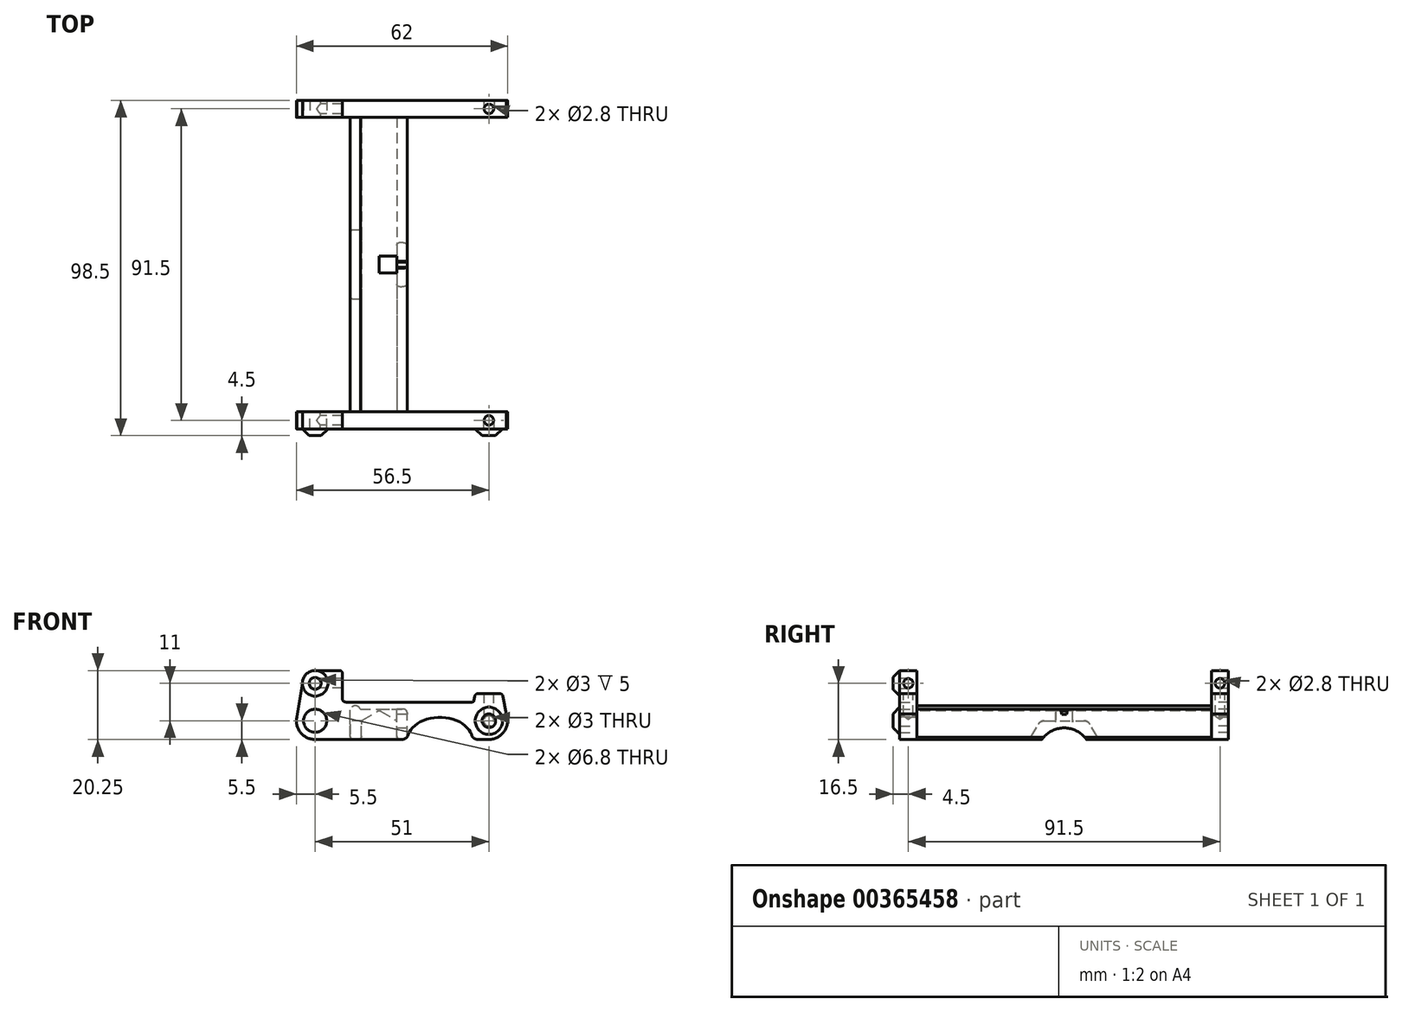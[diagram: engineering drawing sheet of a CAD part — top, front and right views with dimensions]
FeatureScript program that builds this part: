
annotation { "Feature Type Name" : "Feature", "Feature Type Description" : "" }
export const myFeature = defineFeature(function(context is Context, id is Id, definition is map)
    precondition{}
    {
        {
            var Q0;
            Q0=qCreatedBy(makeId("Front.planeOp"),FACE);
            var sketch = newSketch(context, id + "F0", { "sketchPlane" : qUnion([Q0])});
            skCircle(sketch, "E0", {"center": v(0, 0) * mm, "radius": 3.4 * mm});
            skCircle(sketch, "E1", {"center": v(0, 11) * mm, "radius": 1.5 * mm});
            skCircle(sketch, "E2", {"center": v(51, 0) * mm, "radius": 1.5 * mm});
            skArc(sketch, "E3", {"start": v(-5.35, 1.3) * mm, "mid": v(-4.32, -3.4) * mm, "end": v(0, -5.5) * mm});
            skLineSegment(sketch, "E4", {"start": v(0, -5.5) * mm, "end": v(51, -5.5) * mm});
            skArc(sketch, "E5", {"start": v(51, -5.5) * mm, "mid": v(56.5, 0) * mm, "end": v(51, 5.5) * mm});
            skLineSegment(sketch, "E6", {"start": v(9, 5.5) * mm, "end": v(46.12, 5.5) * mm});
            skPoint(sketch, "E7.orphan", {"position": v(0, 5.5) * mm});
            skPoint(sketch, "E8.orphan", {"position": v(-5.66, 0) * mm});
            skPoint(sketch, "E9.visualSharp", {"position": v(4.33, 5.5) * mm});
            skLineSegment(sketch, "E10", {"start": v(51, 1.5) * mm, "end": v(51, 5.5) * mm});
            skLineSegment(sketch, "E11", {"start": v(51, 0) * mm, "end": v(51, 8) * mm});
            skLineSegment(sketch, "E12", {"start": v(51, 8) * mm, "end": v(47.83, 8) * mm});
            skLineSegment(sketch, "E13", {"start": v(51, 8) * mm, "end": v(54.17, 8) * mm});
            skLineSegment(sketch, "E14", {"start": v(55.15, 7.18) * mm, "end": v(56.13, 2) * mm});
            skPoint(sketch, "E15.orphan", {"position": v(56.5, 0) * mm});
            skLineSegment(sketch, "E16.MirrorCS", {"start": v(46.85, 7.18) * mm, "end": v(46.6, 5.9) * mm});
            skPoint(sketch, "E17.visualSharp", {"position": v(55, 8) * mm});
            skArc(sketch, "E17.filletArc", {"start": v(55.15, 7.18) * mm, "mid": v(54.8, 7.77) * mm, "end": v(54.17, 8) * mm});
            skPoint(sketch, "E18.visualSharp", {"position": v(47, 8) * mm});
            skArc(sketch, "E18.filletArc", {"start": v(47.83, 8) * mm, "mid": v(47.2, 7.77) * mm, "end": v(46.85, 7.18) * mm});
            skPoint(sketch, "E19.orphan", {"position": v(45.87, 2) * mm});
            skArc(sketch, "E20.filletArc", {"start": v(46.12, 5.5) * mm, "mid": v(46.44, 5.62) * mm, "end": v(46.6, 5.9) * mm});
            skLineSegment(sketch, "E21", {"start": v(0, 11) * mm, "end": v(1.5, 11) * mm});
            skLineSegment(sketch, "E22", {"start": v(8, 11) * mm, "end": v(8, 14) * mm});
            skPoint(sketch, "E22.endSnap0", {"position": v(0, 14) * mm});
            skLineSegment(sketch, "E23", {"start": v(8, 11) * mm, "end": v(8, 6.5) * mm});
            skArc(sketch, "E24", {"start": v(0, 14.75) * mm, "mid": v(-2.65, 13.65) * mm, "end": v(-3.75, 11) * mm});
            skLineSegment(sketch, "E25", {"start": v(-3.75, 11) * mm, "end": v(-5.35, 1.3) * mm});
            skLineSegment(sketch, "E26", {"start": v(0, 11) * mm, "end": v(0, 14.75) * mm});
            skLineSegment(sketch, "E27", {"start": v(0, 14.75) * mm, "end": v(7.2, 14.75) * mm});
            skLineSegment(sketch, "E28", {"start": v(8, 13.95) * mm, "end": v(8, 11) * mm});
            skPoint(sketch, "E29.visualSharp", {"position": v(8, 14.75) * mm});
            skArc(sketch, "E29.filletArc", {"start": v(8, 13.95) * mm, "mid": v(7.77, 14.52) * mm, "end": v(7.2, 14.75) * mm});
            skPoint(sketch, "E30.visualSharp", {"position": v(8, 5.5) * mm});
            skArc(sketch, "E30.filletArc", {"start": v(8, 6.5) * mm, "mid": v(8.3, 5.8) * mm, "end": v(9, 5.5) * mm});
            skSolve(sketch);
        }
        {
            var Q0;
            Q0=qSketchRegion(id+"F0",true);
            extrude(context, id + "F1", {"entities" : qUnion([Q0]), "depth" : 5 * mm});
        }
        {
            var Q0;
            Q0=makeQuery(id+"F1.opExtrude","CAP_FACE",FACE,{"disambiguationData":[OSD([sQuery(id+"F0.wireOp",EDGE,"E0"),sQuery(id+"F0.wireOp",EDGE,"E1"),sQuery(id+"F0.wireOp",EDGE,"E2"),sQuery(id+"F0.wireOp",EDGE,"E3"),sQuery(id+"F0.wireOp",EDGE,"E4"),sQuery(id+"F0.wireOp",EDGE,"mQrOnHyL-yETB-5Hyz-XC6m-Qhvp57tjZrM2"),sQuery(id+"F0.wireOp",EDGE,"GuxY412t-x2rp-MWa2-55Ok-ayXwRCNW1Ffh"),sQuery(id+"F0.wireOp",EDGE,"Tq4Ys5zz-jUqY-a6fJ-V2RF-rb2bUuLUyHlJ"),sQuery(id+"F0.wireOp",EDGE,"E5"),sQuery(id+"F0.wireOp",EDGE,"E6"),sQuery(id+"F0.wireOp",EDGE,"E9.filletArc")])],"isStart":true});
            var sketch = newSketch(context, id + "F2", { "sketchPlane" : qUnion([Q0])});
            skLineSegment(sketch, "E31.MirrorCS", {"start": v(-25.5, 3.4) * mm, "end": v(-20.3, 3.4) * mm});
            skPoint(sketch, "E32.end.orphan", {"position": v(-27, 0) * mm});
            skPoint(sketch, "E32.start.orphan", {"position": v(-27, 3.4) * mm});
            skLineSegment(sketch, "E33", {"start": v(0, 0) * mm, "end": v(0, 3.4) * mm});
            skLineSegment(sketch, "E34", {"start": v(-27, -5.5) * mm, "end": v(-27, 3.4) * mm});
            skLineSegment(sketch, "E35", {"start": v(-24, -5.5) * mm, "end": v(-24, 0) * mm});
            skLineSegment(sketch, "E36", {"start": v(-27, -5.5) * mm, "end": v(-24, -5.5) * mm});
            skLineSegment(sketch, "E37", {"start": v(-24, 0) * mm, "end": v(-18.8, 3) * mm});
            skLineSegment(sketch, "E38", {"start": v(-27, 3.4) * mm, "end": v(-25.5, 3.4) * mm});
            skLineSegment(sketch, "E39", {"start": v(-20.3, 3.4) * mm, "end": v(-18.8, 3.4) * mm});
            skLineSegment(sketch, "E40.MirrorCS", {"start": v(-13.6, 0) * mm, "end": v(-18.8, 3) * mm});
            skLineSegment(sketch, "E41.MirrorCS", {"start": v(-13.6, -5.5) * mm, "end": v(-13.6, 0) * mm});
            skLineSegment(sketch, "E42.MirrorCS", {"start": v(-10.6, -5.5) * mm, "end": v(-13.6, -5.5) * mm});
            skLineSegment(sketch, "E43.MirrorCS", {"start": v(-10.3, -5.5) * mm, "end": v(-10.3, 3.4) * mm});
            skLineSegment(sketch, "E44.MirrorCS", {"start": v(-17.3, 3.4) * mm, "end": v(-18.8, 3.4) * mm});
            skArc(sketch, "E45", {"start": v(-10.3, 3.4) * mm, "mid": v(-11.8, 4.4) * mm, "end": v(-13.3, 3.4) * mm});
            skLineSegment(sketch, "E46.trimOffspring", {"start": v(-13.3, 3.4) * mm, "end": v(-17.3, 3.4) * mm});
            skLineSegment(sketch, "E47", {"start": v(-10.6, -5.5) * mm, "end": v(-10.3, -5.5) * mm});
            skSolve(sketch);
        }
        {
            var Q0;
            Q0=qSketchRegion(id+"F2",true);
            extrude(context, id + "F3", {"entities" : qUnion([Q0]), "operationType" : NewBodyOperationType.ADD, "depth" : 86.5 * mm});
        }
        {
            var Q0;
            Q0=makeQuery(id+"F3.opExtrude","SWEPT_EDGE",EDGE,{"disambiguationData":[OSD([sQuery(id+"F2.wireOp",EDGE,"E35"),sQuery(id+"F2.wireOp",EDGE,"E37")])]});
            var Q1;
            Q1=makeQuery(id+"F3.opExtrude","SWEPT_EDGE",EDGE,{"disambiguationData":[OSD([sQuery(id+"F2.wireOp",EDGE,"E40.MirrorCS"),sQuery(id+"F2.wireOp",EDGE,"E41.MirrorCS")])]});
            fillet(context, id + "F4", {"entities" : qUnion([Q0, Q1]), "radius" : 0.8 * mm, "tangentPropagation" : true, "allowEdgeOverflow" : false});
        }
        {
            var Q0;
            {var subQ0=sQuery(id+"F0.wireOp",EDGE,"E30.filletArc");var subQ1=sQuery(id+"F0.wireOp",EDGE,"E29.filletArc");var subQ2=sQuery(id+"F0.wireOp",EDGE,"E27");var subQ3=sQuery(id+"F0.wireOp",EDGE,"E25");var subQ4=sQuery(id+"F0.wireOp",EDGE,"E24");var subQ5=sQuery(id+"F0.wireOp",EDGE,"E28");var subQ6=sQuery(id+"F0.wireOp",EDGE,"E23");var subQ7=sQuery(id+"F0.wireOp",EDGE,"E20.filletArc");var subQ8=sQuery(id+"F0.wireOp",EDGE,"E18.filletArc");var subQ9=sQuery(id+"F0.wireOp",EDGE,"E17.filletArc");var subQ10=sQuery(id+"F0.wireOp",EDGE,"E2");var subQ11=sQuery(id+"F0.wireOp",EDGE,"E1");var subQ12=sQuery(id+"F0.wireOp",EDGE,"E3");var subQ13=sQuery(id+"F0.wireOp",EDGE,"E0");var subQ14=sQuery(id+"F0.wireOp",EDGE,"E16.MirrorCS");var subQ15=sQuery(id+"F0.wireOp",EDGE,"E4");var subQ16=sQuery(id+"F0.wireOp",EDGE,"E5");var subQ17=sQuery(id+"F0.wireOp",EDGE,"E6");var subQ18=sQuery(id+"F0.wireOp",EDGE,"E13");var subQ19=sQuery(id+"F0.wireOp",EDGE,"E12");var subQ20=sQuery(id+"F0.wireOp",EDGE,"E14");Q0=makeQuery(id+"F3.boolean.opBoolean","SPLIT",FACE,{"disambiguationData":[TD([makeQuery(id+"F1.opExtrude","SWEPT_FACE",FACE,{"disambiguationData":[OSD([subQ13])]})])],"derivedFrom":makeQuery(id+"F1.opExtrude","CAP_FACE",FACE,{"disambiguationData":[OSD([subQ13,subQ11,subQ10,subQ12,subQ15,subQ16,subQ17,subQ19,subQ18,subQ20,subQ14,subQ9,subQ8,subQ7,subQ6,subQ4,subQ3,subQ2,subQ5,subQ1,subQ0])],"isStart":true})});}
            cPlane(context, id + "F5", {"entities" : qUnion([Q0]), "cplaneType" : CPlaneType.OFFSET, "offset" : (86.5 / 2) * mm, "width" : 150 * mm, "height" : 150 * mm});
        }
        {
            var Q0;
            Q0=makeQuery(id+"F1.opExtrude","SWEPT_BODY",BODY,{"disambiguationData":[OSD([sQuery(id+"F0.wireOp",EDGE,"E0"),sQuery(id+"F0.wireOp",EDGE,"E1"),sQuery(id+"F0.wireOp",EDGE,"E2"),sQuery(id+"F0.wireOp",EDGE,"E3"),sQuery(id+"F0.wireOp",EDGE,"E4"),sQuery(id+"F0.wireOp",EDGE,"mQrOnHyL-yETB-5Hyz-XC6m-Qhvp57tjZrM2"),sQuery(id+"F0.wireOp",EDGE,"GuxY412t-x2rp-MWa2-55Ok-ayXwRCNW1Ffh"),sQuery(id+"F0.wireOp",EDGE,"Tq4Ys5zz-jUqY-a6fJ-V2RF-rb2bUuLUyHlJ"),sQuery(id+"F0.wireOp",EDGE,"E5"),sQuery(id+"F0.wireOp",EDGE,"E6"),sQuery(id+"F0.wireOp",EDGE,"E9.filletArc")])]});
            var Q1;
            Q1=qCreatedBy(id+"F5.planeOp",FACE);
            mirror(context, id + "F6", {"operationType" : NewBodyOperationType.ADD, "entities" : qUnion([Q0]), "mirrorPlane" : qUnion([Q1])});
        }
        {
            var Q0;
            Q0=makeQuery(id+"F1.opExtrude","CAP_FACE",FACE,{"disambiguationData":[OSD([sQuery(id+"F0.wireOp",EDGE,"E0"),sQuery(id+"F0.wireOp",EDGE,"E1"),sQuery(id+"F0.wireOp",EDGE,"E2"),sQuery(id+"F0.wireOp",EDGE,"E3"),sQuery(id+"F0.wireOp",EDGE,"E4"),sQuery(id+"F0.wireOp",EDGE,"mQrOnHyL-yETB-5Hyz-XC6m-Qhvp57tjZrM2"),sQuery(id+"F0.wireOp",EDGE,"GuxY412t-x2rp-MWa2-55Ok-ayXwRCNW1Ffh"),sQuery(id+"F0.wireOp",EDGE,"Tq4Ys5zz-jUqY-a6fJ-V2RF-rb2bUuLUyHlJ"),sQuery(id+"F0.wireOp",EDGE,"E5"),sQuery(id+"F0.wireOp",EDGE,"E6"),sQuery(id+"F0.wireOp",EDGE,"E9.filletArc")])],"isStart":false});
            var sketch = newSketch(context, id + "F7", { "sketchPlane" : qUnion([Q0])});
            skCircle(sketch, "E48", {"center": v(51, 0) * mm, "radius": 4 * mm});
            skSolve(sketch);
        }
        {
            var Q0;
            Q0=qSketchRegion(id+"F7",true);
            extrude(context, id + "F8", {"entities" : qUnion([Q0]), "operationType" : NewBodyOperationType.ADD, "depth" : 2 * mm, "hasDraft" : true, "draftAngle" : 45 * degree, "draftPullDirection" : true});
        }
        {
            var Q0;
            Q0=qCreatedBy(makeId("Right.planeOp"),FACE);
            var sketch = newSketch(context, id + "F9", { "sketchPlane" : qUnion([Q0])});
            skLineSegment(sketch, "E49", {"start": v(0, 0) * mm, "end": v(0, 11) * mm});
            skLineSegment(sketch, "E50", {"start": v(0, 11) * mm, "end": v(-2.5, 11) * mm});
            skCircle(sketch, "E51", {"center": v(-2.5, 11) * mm, "radius": 1.4 * mm});
            skLineSegment(sketch, "E52", {"start": v(0, 0) * mm, "end": v(43.25, 0) * mm});
            skLineSegment(sketch, "E53", {"start": v(43.25, 0) * mm, "end": v(86.5, 0) * mm});
            skLineSegment(sketch, "E54", {"start": v(86.5, 0) * mm, "end": v(86.5, 11.55) * mm});
            skLineSegment(sketch, "E55", {"start": v(43.25, 0) * mm, "end": v(43.25, 6.9) * mm});
            skCircle(sketch, "E56.MirrorC", {"center": v(89, 11) * mm, "radius": 1.4 * mm});
            skSolve(sketch);
        }
        {
            var Q0;
            Q0=qSketchRegion(id+"F9",true);
            extrude(context, id + "F10", {"entities" : qUnion([Q0]), "operationType" : NewBodyOperationType.REMOVE, "depth" : 25 * mm});
        }
        {
            var Q0;
            Q0=makeQuery(id+"F6.opPattern","COPY",FACE,{"derivedFrom":makeQuery(id+"F1.opExtrude","SWEPT_FACE",FACE,{"disambiguationData":[OSD([sQuery(id+"F0.wireOp",EDGE,"E12"),sQuery(id+"F0.wireOp",EDGE,"E13")])]}),"instanceName":"1"});
            var sketch = newSketch(context, id + "F11", { "sketchPlane" : qUnion([Q0])});
            skCircle(sketch, "E57", {"center": v(51, 89) * mm, "radius": 1.4 * mm});
            skPoint(sketch, "E57.centerSnap0", {"position": v(54.17, 89) * mm});
            skPoint(sketch, "E57.centerSnap1", {"position": v(51, 86.5) * mm});
            skCircle(sketch, "E58.MirrorC", {"center": v(51, -2.5) * mm, "radius": 1.4 * mm});
            skSolve(sketch);
        }
        {
            var Q0;
            Q0=qSketchRegion(id+"F11",true);
            extrude(context, id + "F12", {"entities" : qUnion([Q0]), "operationType" : NewBodyOperationType.REMOVE, "oppositeDirection" : true, "depth" : 8 * mm});
        }
        {
            var Q0;
            Q0=makeQuery(id+"F1.opExtrude","CAP_FACE",FACE,{"disambiguationData":[OSD([sQuery(id+"F0.wireOp",EDGE,"E0"),sQuery(id+"F0.wireOp",EDGE,"E1"),sQuery(id+"F0.wireOp",EDGE,"E2"),sQuery(id+"F0.wireOp",EDGE,"E3"),sQuery(id+"F0.wireOp",EDGE,"E4"),sQuery(id+"F0.wireOp",EDGE,"E5"),sQuery(id+"F0.wireOp",EDGE,"E6"),sQuery(id+"F0.wireOp",EDGE,"E12"),sQuery(id+"F0.wireOp",EDGE,"E13"),sQuery(id+"F0.wireOp",EDGE,"E14"),sQuery(id+"F0.wireOp",EDGE,"E16.MirrorCS"),sQuery(id+"F0.wireOp",EDGE,"E17.filletArc"),sQuery(id+"F0.wireOp",EDGE,"E18.filletArc"),sQuery(id+"F0.wireOp",EDGE,"E20.filletArc"),sQuery(id+"F0.wireOp",EDGE,"E23"),sQuery(id+"F0.wireOp",EDGE,"E24"),sQuery(id+"F0.wireOp",EDGE,"E25"),sQuery(id+"F0.wireOp",EDGE,"E27"),sQuery(id+"F0.wireOp",EDGE,"E28"),sQuery(id+"F0.wireOp",EDGE,"E29.filletArc"),sQuery(id+"F0.wireOp",EDGE,"E30.filletArc")])],"isStart":false});
            var sketch = newSketch(context, id + "F13", { "sketchPlane" : qUnion([Q0])});
            skCircle(sketch, "E59", {"center": v(0, 11) * mm, "radius": 3.75 * mm});
            skSolve(sketch);
        }
        {
            var Q0;
            Q0=qSketchRegion(id+"F13",true);
            extrude(context, id + "F14", {"entities" : qUnion([Q0]), "operationType" : NewBodyOperationType.ADD, "depth" : 2 * mm, "hasDraft" : true, "draftAngle" : 45 * degree, "draftPullDirection" : true});
        }
        {
            var Q0;
            Q0=makeQuery(id+"F3.opExtrude","SWEPT_EDGE",EDGE,{"disambiguationData":[OSD([sQuery(id+"F2.wireOp",EDGE,"E37"),sQuery(id+"F2.wireOp",EDGE,"E40.MirrorCS")])]});
            var Q1;
            Q1=makeQuery(id+"F3.opExtrude","SWEPT_EDGE",EDGE,{"disambiguationData":[OSD([sQuery(id+"F2.wireOp",EDGE,"E34"),sQuery(id+"F2.wireOp",EDGE,"E38")])]});
            var Q2;
            Q2=makeQuery(id+"F3.opExtrude","SWEPT_EDGE",EDGE,{"disambiguationData":[OSD([sQuery(id+"F0.wireOp",EDGE,"E4"),sQuery(id+"F2.wireOp",EDGE,"E34"),sQuery(id+"F2.wireOp",EDGE,"E36")])]});
            var Q3;
            Q3=makeQuery(id+"F3.opExtrude","SWEPT_EDGE",EDGE,{"disambiguationData":[OSD([sQuery(id+"F0.wireOp",EDGE,"E4"),sQuery(id+"F2.wireOp",EDGE,"E35"),sQuery(id+"F2.wireOp",EDGE,"E36")])]});
            var Q4;
            Q4=makeQuery(id+"F3.opExtrude","SWEPT_EDGE",EDGE,{"disambiguationData":[OSD([sQuery(id+"F0.wireOp",EDGE,"E4"),sQuery(id+"F2.wireOp",EDGE,"E41.MirrorCS"),sQuery(id+"F2.wireOp",EDGE,"E42.MirrorCS")])]});
            var Q5;
            Q5=makeQuery(id+"F3.opExtrude","SWEPT_EDGE",EDGE,{"disambiguationData":[OSD([sQuery(id+"F0.wireOp",EDGE,"E4"),sQuery(id+"F2.wireOp",EDGE,"E43.MirrorCS"),sQuery(id+"F2.wireOp",EDGE,"E47")])]});
            fillet(context, id + "F15", {"entities" : qUnion([Q0, Q1, Q2, Q3, Q4, Q5]), "radius" : 1 * mm, "tangentPropagation" : true, "allowEdgeOverflow" : false});
        }
        {
            var Q0;
            Q0=makeQuery(id+"F3.opExtrude","SWEPT_FACE",FACE,{"disambiguationData":[OSD([sQuery(id+"F2.wireOp",EDGE,"E43.MirrorCS")])]});
            var sketch = newSketch(context, id + "F16", { "sketchPlane" : qUnion([Q0])});
            skLineSegment(sketch, "E60", {"start": v(-43.25, -1.5) * mm, "end": v(-43.25, 0) * mm});
            skLineSegment(sketch, "E61", {"start": v(-43.25, 0) * mm, "end": v(-36.25, 0) * mm});
            skLineSegment(sketch, "E62", {"start": v(-36.25, 0) * mm, "end": v(-32.12, -7.16) * mm});
            skLineSegment(sketch, "E63.MirrorCS", {"start": v(-43.25, 0) * mm, "end": v(-50.25, 0) * mm});
            skLineSegment(sketch, "E64.MirrorCS", {"start": v(-50.25, 0) * mm, "end": v(-54.38, -7.16) * mm});
            skLineSegment(sketch, "E65", {"start": v(-54.38, -7.16) * mm, "end": v(-32.12, -7.16) * mm});
            skSolve(sketch);
        }
        {
            var Q0;
            Q0=qSketchRegion(id+"F16",true);
            extrude(context, id + "F17", {"entities" : qUnion([Q0]), "operationType" : NewBodyOperationType.REMOVE, "oppositeDirection" : true, "depth" : 10 * mm});
        }
        {
            var Q0;
            Q0=makeQuery(id+"F17.boolean.opBoolean","COPY",EDGE,{"derivedFrom":makeQuery(id+"F17.opExtrude","SWEPT_EDGE",EDGE,{"disambiguationData":[OSD([sQuery(id+"F16.wireOp",EDGE,"E63.MirrorCS"),sQuery(id+"F16.wireOp",EDGE,"E64.MirrorCS")])]})});
            var Q1;
            Q1=makeQuery(id+"F17.boolean.opBoolean","COPY",EDGE,{"derivedFrom":makeQuery(id+"F17.opExtrude","SWEPT_EDGE",EDGE,{"disambiguationData":[OSD([sQuery(id+"F16.wireOp",EDGE,"E61"),sQuery(id+"F16.wireOp",EDGE,"E62")])]})});
            fillet(context, id + "F18", {"entities" : qUnion([Q0, Q1]), "radius" : 2 * mm, "tangentPropagation" : true, "allowEdgeOverflow" : false});
        }
        {
            var Q0;
            Q0=makeQuery(id+"F1.opExtrude","CAP_FACE",FACE,{"disambiguationData":[OSD([sQuery(id+"F0.wireOp",EDGE,"E0"),sQuery(id+"F0.wireOp",EDGE,"E1"),sQuery(id+"F0.wireOp",EDGE,"E2"),sQuery(id+"F0.wireOp",EDGE,"E3"),sQuery(id+"F0.wireOp",EDGE,"E4"),sQuery(id+"F0.wireOp",EDGE,"E5"),sQuery(id+"F0.wireOp",EDGE,"E6"),sQuery(id+"F0.wireOp",EDGE,"E12"),sQuery(id+"F0.wireOp",EDGE,"E13"),sQuery(id+"F0.wireOp",EDGE,"E14"),sQuery(id+"F0.wireOp",EDGE,"E16.MirrorCS"),sQuery(id+"F0.wireOp",EDGE,"E17.filletArc"),sQuery(id+"F0.wireOp",EDGE,"E18.filletArc"),sQuery(id+"F0.wireOp",EDGE,"E20.filletArc"),sQuery(id+"F0.wireOp",EDGE,"E23"),sQuery(id+"F0.wireOp",EDGE,"E24"),sQuery(id+"F0.wireOp",EDGE,"E25"),sQuery(id+"F0.wireOp",EDGE,"E27"),sQuery(id+"F0.wireOp",EDGE,"E28"),sQuery(id+"F0.wireOp",EDGE,"E29.filletArc"),sQuery(id+"F0.wireOp",EDGE,"E30.filletArc")])],"isStart":false});
            var sketch = newSketch(context, id + "F19", { "sketchPlane" : qUnion([Q0])});
            skLineSegment(sketch, "E66", {"start": v(46.12, 5.5) * mm, "end": v(46.12, -5.5) * mm});
            skLineSegment(sketch, "E67", {"start": v(46.12, -5.5) * mm, "end": v(27.12, -5.5) * mm});
            skEllipse(sketch, "E68", {"center": v(36.62, -5.5) * mm, "majorRadius": 9.5 * mm, "minorRadius": 6.5 * mm, "majorAxis": v(1, 0)});
            skSolve(sketch);
        }
        {
            var Q0;
            Q0=qSketchRegion(id+"F19",true);
            extrude(context, id + "F20", {"entities" : qUnion([Q0]), "operationType" : NewBodyOperationType.REMOVE, "oppositeDirection" : true, "depth" : 108.2 * mm});
        }
        {
            var Q0;
            {var subQ0=makeQuery(id+"F3.boolean.opBoolean","MERGE",FACE,{"derivedFrom":[makeQuery(id+"F1.opExtrude","SWEPT_FACE",FACE,{"disambiguationData":[OSD([sQuery(id+"F0.wireOp",EDGE,"E4")])]}),makeQuery(id+"F3.opExtrude","SWEPT_FACE",FACE,{"disambiguationData":[OSD([sQuery(id+"F2.wireOp",EDGE,"E36")])]}),makeQuery(id+"F3.opExtrude","SWEPT_FACE",FACE,{"disambiguationData":[OSD([sQuery(id+"F2.wireOp",EDGE,"E42.MirrorCS"),sQuery(id+"F2.wireOp",EDGE,"E47")])]})]});Q0=makeQuery(id+"F20.boolean.opBoolean","INTERSECT",EDGE,{"disambiguationData":[OD(2.0)],"derivedFrom":[makeQuery(id+"F6.boolean.opBoolean","MERGE",FACE,{"derivedFrom":[subQ0,makeQuery(id+"F6.opPattern","COPY",FACE,{"derivedFrom":subQ0,"instanceName":"1"})]}),makeQuery(id+"F20.opExtrude","SWEPT_FACE",FACE,{"disambiguationData":[OSD([sQuery(id+"F19.wireOp",EDGE,"E68")])]})]});}
            var Q1;
            {var subQ0=makeQuery(id+"F3.boolean.opBoolean","MERGE",FACE,{"derivedFrom":[makeQuery(id+"F1.opExtrude","SWEPT_FACE",FACE,{"disambiguationData":[OSD([sQuery(id+"F0.wireOp",EDGE,"E4")])]}),makeQuery(id+"F3.opExtrude","SWEPT_FACE",FACE,{"disambiguationData":[OSD([sQuery(id+"F2.wireOp",EDGE,"E36")])]}),makeQuery(id+"F3.opExtrude","SWEPT_FACE",FACE,{"disambiguationData":[OSD([sQuery(id+"F2.wireOp",EDGE,"E42.MirrorCS"),sQuery(id+"F2.wireOp",EDGE,"E47")])]})]});Q1=makeQuery(id+"F20.boolean.opBoolean","INTERSECT",EDGE,{"disambiguationData":[OD(0.0)],"derivedFrom":[makeQuery(id+"F6.boolean.opBoolean","MERGE",FACE,{"derivedFrom":[subQ0,makeQuery(id+"F6.opPattern","COPY",FACE,{"derivedFrom":subQ0,"instanceName":"1"})]}),makeQuery(id+"F20.opExtrude","SWEPT_FACE",FACE,{"disambiguationData":[OSD([sQuery(id+"F19.wireOp",EDGE,"E68")])]})]});}
            var Q2;
            {var subQ0=makeQuery(id+"F3.boolean.opBoolean","MERGE",FACE,{"derivedFrom":[makeQuery(id+"F1.opExtrude","SWEPT_FACE",FACE,{"disambiguationData":[OSD([sQuery(id+"F0.wireOp",EDGE,"E4")])]}),makeQuery(id+"F3.opExtrude","SWEPT_FACE",FACE,{"disambiguationData":[OSD([sQuery(id+"F2.wireOp",EDGE,"E36")])]}),makeQuery(id+"F3.opExtrude","SWEPT_FACE",FACE,{"disambiguationData":[OSD([sQuery(id+"F2.wireOp",EDGE,"E42.MirrorCS"),sQuery(id+"F2.wireOp",EDGE,"E47")])]})]});Q2=makeQuery(id+"F20.boolean.opBoolean","INTERSECT",EDGE,{"disambiguationData":[OD(1.0)],"derivedFrom":[makeQuery(id+"F6.boolean.opBoolean","MERGE",FACE,{"derivedFrom":[subQ0,makeQuery(id+"F6.opPattern","COPY",FACE,{"derivedFrom":subQ0,"instanceName":"1"})]}),makeQuery(id+"F20.opExtrude","SWEPT_FACE",FACE,{"disambiguationData":[OSD([sQuery(id+"F19.wireOp",EDGE,"E68")])]})]});}
            var Q3;
            {var subQ0=makeQuery(id+"F3.boolean.opBoolean","MERGE",FACE,{"derivedFrom":[makeQuery(id+"F1.opExtrude","SWEPT_FACE",FACE,{"disambiguationData":[OSD([sQuery(id+"F0.wireOp",EDGE,"E4")])]}),makeQuery(id+"F3.opExtrude","SWEPT_FACE",FACE,{"disambiguationData":[OSD([sQuery(id+"F2.wireOp",EDGE,"E36")])]}),makeQuery(id+"F3.opExtrude","SWEPT_FACE",FACE,{"disambiguationData":[OSD([sQuery(id+"F2.wireOp",EDGE,"E42.MirrorCS"),sQuery(id+"F2.wireOp",EDGE,"E47")])]})]});Q3=makeQuery(id+"F20.boolean.opBoolean","INTERSECT",EDGE,{"disambiguationData":[OD(3.0)],"derivedFrom":[makeQuery(id+"F6.boolean.opBoolean","MERGE",FACE,{"derivedFrom":[subQ0,makeQuery(id+"F6.opPattern","COPY",FACE,{"derivedFrom":subQ0,"instanceName":"1"})]}),makeQuery(id+"F20.opExtrude","SWEPT_FACE",FACE,{"disambiguationData":[OSD([sQuery(id+"F19.wireOp",EDGE,"E68")])]})]});}
            fillet(context, id + "F21", {"entities" : qUnion([Q0, Q1, Q2, Q3]), "radius" : 2 * mm, "tangentPropagation" : true, "allowEdgeOverflow" : false});
        }
        {
            var Q0;
            Q0=makeQuery(id+"F3.opExtrude","SWEPT_FACE",FACE,{"disambiguationData":[OSD([sQuery(id+"F2.wireOp",EDGE,"E31.MirrorCS"),sQuery(id+"F2.wireOp",EDGE,"E38"),sQuery(id+"F2.wireOp",EDGE,"E39"),sQuery(id+"F2.wireOp",EDGE,"E44.MirrorCS"),sQuery(id+"F2.wireOp",EDGE,"E46.trimOffspring")])]});
            var sketch = newSketch(context, id + "F22", { "sketchPlane" : qUnion([Q0])});
            skLineSegment(sketch, "E69", {"start": v(0, 0) * mm, "end": v(0, 43.25) * mm});
            skPoint(sketch, "E69.endSnap0", {"position": v(18.15, 43.25) * mm});
            skLineSegment(sketch, "E70", {"start": v(0, 43.25) * mm, "end": v(24, 43.25) * mm});
            skLineSegment(sketch, "E71", {"start": v(24, 43.25) * mm, "end": v(24, 45.75) * mm});
            skLineSegment(sketch, "E72", {"start": v(24, 45.75) * mm, "end": v(18.8, 45.75) * mm});
            skLineSegment(sketch, "E73", {"start": v(18.8, 45.75) * mm, "end": v(18.8, 40.75) * mm});
            skLineSegment(sketch, "E74", {"start": v(18.8, 40.75) * mm, "end": v(24, 40.75) * mm});
            skLineSegment(sketch, "E75", {"start": v(24, 40.75) * mm, "end": v(24, 43.25) * mm});
            skSolve(sketch);
        }
        {
            var Q0;
            Q0 = qSketchRegion(id + "F22", true);
            extrude(context, id + "F23", {"entities" : qUnion([Q0]), "operationType" : NewBodyOperationType.REMOVE, "oppositeDirection" : true, "depth" : 25 * mm});
        }
        {
            var Q0;
            Q0=makeQuery(id+"F23.boolean.opBoolean","MERGE",FACE,{"derivedFrom":[makeQuery(id+"F3.opExtrude","SWEPT_FACE",FACE,{"disambiguationData":[OSD([sQuery(id+"F2.wireOp",EDGE,"E35")])]}),makeQuery(id+"F23.opExtrude","SWEPT_FACE",FACE,{"disambiguationData":[OSD([sQuery(id+"F22.wireOp",EDGE,"E71"),sQuery(id+"F22.wireOp",EDGE,"E75")])]})]});
            var sketch = newSketch(context, id + "F24", { "sketchPlane" : qUnion([Q0])});
            skLineSegment(sketch, "E76", {"start": v(-43.25, 3.4) * mm, "end": v(-44.25, 3.4) * mm});
            skLineSegment(sketch, "E77", {"start": v(-43.25, 3.4) * mm, "end": v(-43.25, 1.9) * mm});
            skLineSegment(sketch, "E78", {"start": v(-43.25, 1.9) * mm, "end": v(-44, 1.9) * mm});
            skLineSegment(sketch, "E79", {"start": v(-44, 1.9) * mm, "end": v(-44.25, 3.4) * mm});
            skLineSegment(sketch, "E80.MirrorCS", {"start": v(-43.25, 1.9) * mm, "end": v(-42.5, 1.9) * mm});
            skLineSegment(sketch, "E81.MirrorCS", {"start": v(-42.5, 1.9) * mm, "end": v(-42.25, 3.4) * mm});
            skLineSegment(sketch, "E82.MirrorCS", {"start": v(-43.25, 3.4) * mm, "end": v(-42.25, 3.4) * mm});
            skSolve(sketch);
        }
        {
            var Q0;
            Q0 = qSketchRegion(id + "F24", true);
            extrude(context, id + "F25", {"entities" : qUnion([Q0]), "operationType" : NewBodyOperationType.REMOVE, "oppositeDirection" : true, "depth" : 25 * mm});
        }
        {
            var Q0;
            Q0=makeQuery(id+"F3.opExtrude","SWEPT_FACE",FACE,{"disambiguationData":[OSD([sQuery(id+"F2.wireOp",EDGE,"E34")])]});
            var sketch = newSketch(context, id + "F26", { "sketchPlane" : qUnion([Q0])});
            skLineSegment(sketch, "E83", {"start": v(43.25, 1.9) * mm, "end": v(43.25, -2.1) * mm});
            skLineSegment(sketch, "E84", {"start": v(43.25, -2.1) * mm, "end": v(43.25, -10.1) * mm});
            skCircle(sketch, "E85", {"center": v(43.25, -10.1) * mm, "radius": 8 * mm});
            skSolve(sketch);
        }
        {
            var Q0;
            Q0 = qSketchRegion(id + "F26", true);
            extrude(context, id + "F27", {"entities" : qUnion([Q0]), "operationType" : NewBodyOperationType.REMOVE, "oppositeDirection" : true, "depth" : 5 * mm});
        }
    });
